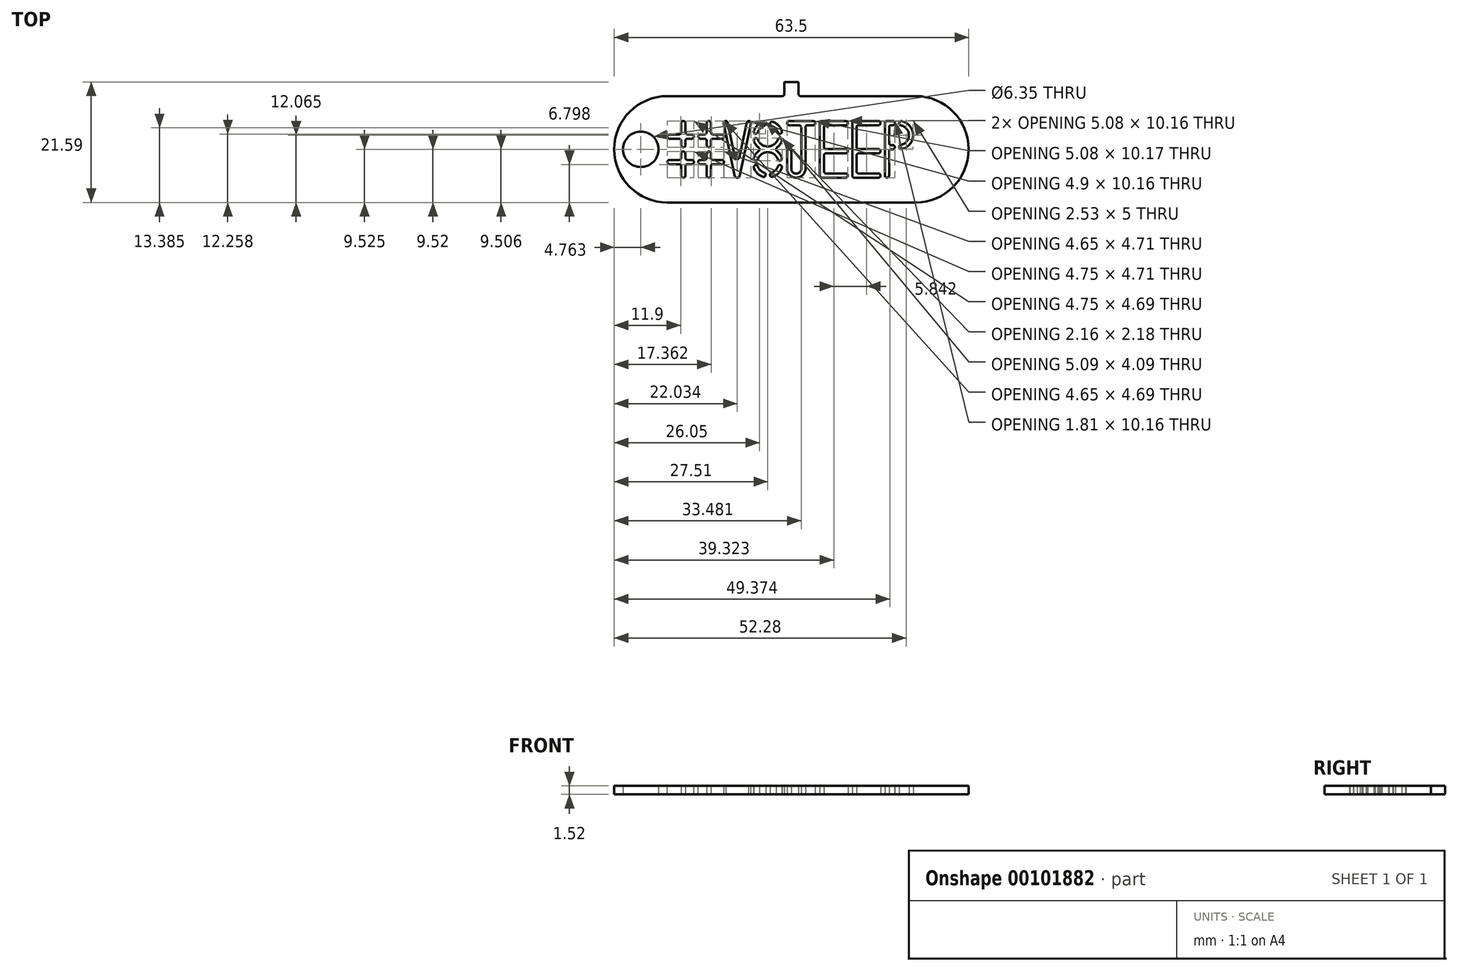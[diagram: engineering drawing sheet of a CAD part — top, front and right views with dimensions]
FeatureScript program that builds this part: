
annotation { "Feature Type Name" : "Feature", "Feature Type Description" : "" }
export const myFeature = defineFeature(function(context is Context, id is Id, definition is map)
    precondition{}
    {
        {
            var Q0;
            Q0=qCreatedBy(makeId("Top.planeOp"),FACE);
            var sketch = newSketch(context, id + "F0", { "sketchPlane" : qUnion([Q0])});
            skLineSegment(sketch, "E0.bottom", {"start": v(0, 0) * mm, "end": v(63.5, 0) * mm, "construction": true});
            skLineSegment(sketch, "E0.top", {"start": v(0, 19.05) * mm, "end": v(63.5, 19.05) * mm, "construction": true});
            skLineSegment(sketch, "E0.left", {"start": v(0, 0) * mm, "end": v(0, 19.05) * mm, "construction": true});
            skLineSegment(sketch, "E0.right", {"start": v(63.5, 0) * mm, "end": v(63.5, 19.05) * mm, "construction": true});
            skCircle(sketch, "E1", {"center": v(9.53, 9.53) * mm, "radius": 9.53 * mm, "construction": true});
            skCircle(sketch, "E2", {"center": v(53.97, 9.53) * mm, "radius": 9.53 * mm, "construction": true});
            skArc(sketch, "E3", {"start": v(9.52, 19.05) * mm, "mid": v(0, 9.53) * mm, "end": v(9.53, 0) * mm});
            skArc(sketch, "E4", {"start": v(53.97, 0) * mm, "mid": v(63.5, 9.53) * mm, "end": v(53.97, 19.05) * mm});
            skLineSegment(sketch, "E5", {"start": v(53.97, 0) * mm, "end": v(9.52, 0) * mm});
            skLineSegment(sketch, "E6.bottom", {"start": v(9.53, 12.2) * mm, "end": v(19.69, 12.2) * mm, "construction": true});
            skLineSegment(sketch, "E6.top", {"start": v(9.53, 11.44) * mm, "end": v(19.69, 11.44) * mm, "construction": true});
            skLineSegment(sketch, "E6.left", {"start": v(9.53, 12.2) * mm, "end": v(9.53, 11.44) * mm, "construction": true});
            skLineSegment(sketch, "E6.right", {"start": v(19.69, 12.2) * mm, "end": v(19.69, 11.44) * mm, "construction": true});
            skLineSegment(sketch, "E7.bottom", {"start": v(9.53, 7.63) * mm, "end": v(19.69, 7.63) * mm, "construction": true});
            skLineSegment(sketch, "E7.top", {"start": v(9.53, 6.86) * mm, "end": v(19.69, 6.86) * mm, "construction": true});
            skLineSegment(sketch, "E7.left", {"start": v(9.53, 7.63) * mm, "end": v(9.53, 6.86) * mm, "construction": true});
            skLineSegment(sketch, "E7.right", {"start": v(19.69, 7.63) * mm, "end": v(19.69, 6.86) * mm, "construction": true});
            skLineSegment(sketch, "E8.bottom", {"start": v(12, 14.6) * mm, "end": v(12.75, 14.6) * mm, "construction": true});
            skLineSegment(sketch, "E8.top", {"start": v(12, 4.44) * mm, "end": v(12.75, 4.44) * mm, "construction": true});
            skLineSegment(sketch, "E8.left", {"start": v(12, 14.6) * mm, "end": v(12, 4.44) * mm, "construction": true});
            skLineSegment(sketch, "E8.right", {"start": v(12.75, 14.6) * mm, "end": v(12.75, 4.44) * mm, "construction": true});
            skLineSegment(sketch, "E9.bottom", {"start": v(16.56, 14.6) * mm, "end": v(17.32, 14.6) * mm, "construction": true});
            skLineSegment(sketch, "E9.top", {"start": v(16.56, 4.44) * mm, "end": v(17.32, 4.44) * mm, "construction": true});
            skLineSegment(sketch, "E9.left", {"start": v(16.56, 14.6) * mm, "end": v(16.56, 4.44) * mm, "construction": true});
            skLineSegment(sketch, "E9.right", {"start": v(17.32, 14.6) * mm, "end": v(17.32, 4.44) * mm, "construction": true});
            skLineSegment(sketch, "E10", {"start": v(9.53, 14.6) * mm, "end": v(53.97, 14.6) * mm, "construction": true});
            skLineSegment(sketch, "E11", {"start": v(53.97, 9.53) * mm, "end": v(53.97, 14.6) * mm, "construction": true});
            skLineSegment(sketch, "E12", {"start": v(9.53, 14.6) * mm, "end": v(9.53, 9.53) * mm, "construction": true});
            skLineSegment(sketch, "E13", {"start": v(53.97, 9.53) * mm, "end": v(53.97, 4.45) * mm, "construction": true});
            skLineSegment(sketch, "E14", {"start": v(53.97, 4.45) * mm, "end": v(9.53, 4.45) * mm, "construction": true});
            skLineSegment(sketch, "E15", {"start": v(9.52, 9.53) * mm, "end": v(9.52, 4.45) * mm, "construction": true});
            skLineSegment(sketch, "E16", {"start": v(19.5, 14.6) * mm, "end": v(20.26, 14.6) * mm, "construction": true});
            skLineSegment(sketch, "E17", {"start": v(19.5, 14.6) * mm, "end": v(21.65, 4.44) * mm});
            skLineSegment(sketch, "E18", {"start": v(21.65, 4.45) * mm, "end": v(22.41, 4.45) * mm});
            skLineSegment(sketch, "E19", {"start": v(22.41, 4.44) * mm, "end": v(24.57, 14.6) * mm});
            skLineSegment(sketch, "E20", {"start": v(24.57, 14.6) * mm, "end": v(23.81, 14.6) * mm});
            skLineSegment(sketch, "E21", {"start": v(23.81, 14.6) * mm, "end": v(22.03, 6.32) * mm});
            skLineSegment(sketch, "E22", {"start": v(22.03, 6.32) * mm, "end": v(20.26, 14.6) * mm});
            skCircle(sketch, "E23", {"center": v(27.51, 11.94) * mm, "radius": 2.67 * mm, "construction": true});
            skCircle(sketch, "E24", {"center": v(27.51, 7.11) * mm, "radius": 2.67 * mm, "construction": true});
            skCircle(sketch, "E25", {"center": v(27.51, 11.94) * mm, "radius": 1.9 * mm, "construction": true});
            skCircle(sketch, "E26", {"center": v(27.51, 7.11) * mm, "radius": 1.9 * mm, "construction": true});
            skLineSegment(sketch, "E27", {"start": v(20.26, 14.6) * mm, "end": v(23.81, 14.6) * mm, "construction": true});
            skLineSegment(sketch, "E28", {"start": v(22.03, 14.6) * mm, "end": v(22.03, 4.45) * mm, "construction": true});
            skLineSegment(sketch, "E29", {"start": v(30.94, 14.6) * mm, "end": v(36.02, 14.6) * mm, "construction": true});
            skLineSegment(sketch, "E30", {"start": v(30.94, 14.6) * mm, "end": v(30.94, 4.44) * mm, "construction": true});
            skLineSegment(sketch, "E31", {"start": v(36.02, 14.6) * mm, "end": v(36.02, 4.44) * mm, "construction": true});
            skLineSegment(sketch, "E32", {"start": v(27.51, 14.6) * mm, "end": v(27.51, 4.44) * mm, "construction": true});
            skLineSegment(sketch, "E33", {"start": v(36.78, 14.6) * mm, "end": v(36.78, 4.44) * mm, "construction": true});
            skLineSegment(sketch, "E34", {"start": v(36.78, 4.45) * mm, "end": v(41.86, 4.45) * mm, "construction": true});
            skLineSegment(sketch, "E35", {"start": v(41.86, 4.44) * mm, "end": v(41.86, 14.6) * mm, "construction": true});
            skLineSegment(sketch, "E36", {"start": v(41.86, 14.6) * mm, "end": v(42.63, 14.6) * mm, "construction": true});
            skLineSegment(sketch, "E37", {"start": v(42.63, 14.6) * mm, "end": v(42.63, 4.44) * mm, "construction": true});
            skLineSegment(sketch, "E38", {"start": v(42.63, 4.45) * mm, "end": v(47.7, 4.45) * mm, "construction": true});
            skLineSegment(sketch, "E39", {"start": v(47.7, 4.44) * mm, "end": v(47.7, 14.6) * mm, "construction": true});
            skLineSegment(sketch, "E40", {"start": v(47.7, 14.6) * mm, "end": v(48.47, 14.6) * mm, "construction": true});
            skLineSegment(sketch, "E41", {"start": v(48.47, 14.6) * mm, "end": v(48.47, 4.44) * mm, "construction": true});
            skLineSegment(sketch, "E42", {"start": v(48.47, 4.45) * mm, "end": v(53.55, 4.45) * mm, "construction": true});
            skLineSegment(sketch, "E43", {"start": v(53.55, 4.44) * mm, "end": v(53.55, 14.6) * mm, "construction": true});
            skLineSegment(sketch, "E44", {"start": v(41.86, 13.84) * mm, "end": v(37.55, 13.84) * mm});
            skLineSegment(sketch, "E45", {"start": v(37.55, 13.84) * mm, "end": v(37.55, 9.56) * mm});
            skLineSegment(sketch, "E46", {"start": v(37.55, 9.56) * mm, "end": v(41.86, 9.56) * mm});
            skLineSegment(sketch, "E47", {"start": v(41.86, 9.56) * mm, "end": v(41.86, 8.8) * mm});
            skLineSegment(sketch, "E48", {"start": v(41.86, 8.8) * mm, "end": v(37.55, 8.8) * mm});
            skLineSegment(sketch, "E49", {"start": v(37.55, 8.8) * mm, "end": v(37.55, 5.2) * mm});
            skLineSegment(sketch, "E50", {"start": v(37.55, 5.2) * mm, "end": v(41.86, 5.2) * mm});
            skLineSegment(sketch, "E51", {"start": v(41.86, 5.2) * mm, "end": v(41.86, 4.45) * mm});
            skLineSegment(sketch, "E52", {"start": v(36.78, 4.44) * mm, "end": v(36.78, 14.6) * mm});
            skLineSegment(sketch, "E53", {"start": v(41.86, 14.6) * mm, "end": v(36.78, 14.6) * mm});
            skLineSegment(sketch, "E54", {"start": v(41.86, 14.6) * mm, "end": v(41.86, 13.84) * mm});
            skLineSegment(sketch, "E55", {"start": v(42.63, 14.6) * mm, "end": v(47.7, 14.6) * mm, "construction": true});
            skLineSegment(sketch, "E56", {"start": v(42.63, 14.6) * mm, "end": v(47.7, 14.6) * mm});
            skLineSegment(sketch, "E57", {"start": v(47.7, 13.84) * mm, "end": v(43.39, 13.84) * mm});
            skLineSegment(sketch, "E58", {"start": v(43.39, 13.84) * mm, "end": v(43.39, 9.56) * mm});
            skLineSegment(sketch, "E59", {"start": v(43.39, 9.56) * mm, "end": v(47.7, 9.56) * mm});
            skLineSegment(sketch, "E60", {"start": v(47.7, 9.56) * mm, "end": v(47.7, 8.8) * mm});
            skLineSegment(sketch, "E61", {"start": v(47.7, 8.8) * mm, "end": v(43.39, 8.8) * mm});
            skLineSegment(sketch, "E62", {"start": v(43.39, 8.8) * mm, "end": v(43.39, 5.2) * mm});
            skLineSegment(sketch, "E63", {"start": v(43.39, 5.2) * mm, "end": v(47.7, 5.2) * mm});
            skLineSegment(sketch, "E64", {"start": v(47.7, 5.2) * mm, "end": v(47.7, 4.45) * mm});
            skLineSegment(sketch, "E65", {"start": v(47.7, 4.45) * mm, "end": v(42.63, 4.44) * mm});
            skLineSegment(sketch, "E66", {"start": v(42.63, 4.44) * mm, "end": v(42.63, 14.6) * mm});
            skLineSegment(sketch, "E67", {"start": v(47.7, 13.84) * mm, "end": v(47.7, 14.6) * mm});
            skLineSegment(sketch, "E68", {"start": v(48.47, 4.44) * mm, "end": v(48.47, 14.6) * mm});
            skLineSegment(sketch, "E69", {"start": v(48.47, 14.6) * mm, "end": v(53.55, 14.6) * mm, "construction": true});
            skLineSegment(sketch, "E70", {"start": v(48.47, 4.45) * mm, "end": v(49.23, 4.45) * mm});
            skLineSegment(sketch, "E71", {"start": v(49.23, 4.44) * mm, "end": v(49.23, 9.52) * mm});
            skLineSegment(sketch, "E72", {"start": v(51, 14.6) * mm, "end": v(51, 9.52) * mm, "construction": true});
            skLineSegment(sketch, "E73", {"start": v(51, 9.52) * mm, "end": v(49.23, 9.52) * mm, "construction": true});
            skArc(sketch, "E74", {"start": v(51, 9.52) * mm, "mid": v(53.55, 12.06) * mm, "end": v(51, 14.6) * mm});
            skLineSegment(sketch, "E75", {"start": v(49.23, 13.84) * mm, "end": v(49.23, 10.29) * mm});
            skLineSegment(sketch, "E76", {"start": v(51, 10.29) * mm, "end": v(51, 13.84) * mm, "construction": true});
            skArc(sketch, "E77", {"start": v(51, 10.29) * mm, "mid": v(52.79, 12.06) * mm, "end": v(51, 13.84) * mm});
            skLineSegment(sketch, "E78", {"start": v(30.94, 9.52) * mm, "end": v(31.7, 9.52) * mm});
            skLineSegment(sketch, "E79", {"start": v(31.7, 9.52) * mm, "end": v(31.7, 5.83) * mm});
            skLineSegment(sketch, "E80", {"start": v(30.94, 5.83) * mm, "end": v(36.02, 5.83) * mm, "construction": true});
            skLineSegment(sketch, "E81", {"start": v(33.48, 5.83) * mm, "end": v(33.48, 13.84) * mm});
            skLineSegment(sketch, "E82", {"start": v(34.24, 5.83) * mm, "end": v(34.24, 13.84) * mm});
            skArc(sketch, "E83", {"start": v(30.94, 5.83) * mm, "mid": v(32.6, 4.43) * mm, "end": v(34.24, 5.83) * mm});
            skArc(sketch, "E84", {"start": v(31.7, 5.83) * mm, "mid": v(32.6, 5.17) * mm, "end": v(33.48, 5.83) * mm});
            skLineSegment(sketch, "E85", {"start": v(30.94, 14.6) * mm, "end": v(36.02, 14.6) * mm});
            skLineSegment(sketch, "E86", {"start": v(30.94, 13.84) * mm, "end": v(36.02, 13.84) * mm, "construction": true});
            skLineSegment(sketch, "E87", {"start": v(30.94, 9.52) * mm, "end": v(30.94, 5.83) * mm});
            skLineSegment(sketch, "E88", {"start": v(34.24, 13.84) * mm, "end": v(36.02, 13.84) * mm});
            skLineSegment(sketch, "E89", {"start": v(36.02, 14.6) * mm, "end": v(36.02, 13.84) * mm});
            skLineSegment(sketch, "E90", {"start": v(30.94, 14.6) * mm, "end": v(30.94, 13.84) * mm});
            skLineSegment(sketch, "E91", {"start": v(33.48, 13.84) * mm, "end": v(30.94, 13.84) * mm});
            skLineSegment(sketch, "E92", {"start": v(12, 14.6) * mm, "end": v(12, 12.2) * mm});
            skLineSegment(sketch, "E93", {"start": v(12, 12.2) * mm, "end": v(9.53, 12.2) * mm});
            skLineSegment(sketch, "E94", {"start": v(9.53, 11.44) * mm, "end": v(12, 11.44) * mm});
            skLineSegment(sketch, "E95", {"start": v(12, 11.44) * mm, "end": v(12, 9.91) * mm});
            skLineSegment(sketch, "E96", {"start": v(12, 14.6) * mm, "end": v(12.75, 14.6) * mm});
            skLineSegment(sketch, "E97", {"start": v(12.75, 12.2) * mm, "end": v(14.28, 12.2) * mm});
            skLineSegment(sketch, "E98", {"start": v(12, 7.63) * mm, "end": v(9.53, 7.63) * mm});
            skLineSegment(sketch, "E99", {"start": v(9.53, 7.63) * mm, "end": v(9.53, 6.86) * mm});
            skLineSegment(sketch, "E100", {"start": v(9.53, 6.86) * mm, "end": v(12, 6.86) * mm});
            skLineSegment(sketch, "E101", {"start": v(12, 6.86) * mm, "end": v(12, 4.44) * mm});
            skLineSegment(sketch, "E102", {"start": v(12.75, 4.44) * mm, "end": v(12.75, 6.86) * mm});
            skLineSegment(sketch, "E103", {"start": v(12.75, 6.86) * mm, "end": v(14.28, 6.86) * mm});
            skLineSegment(sketch, "E104", {"start": v(15.04, 6.86) * mm, "end": v(16.56, 6.86) * mm});
            skLineSegment(sketch, "E105", {"start": v(16.56, 6.86) * mm, "end": v(16.56, 4.44) * mm});
            skLineSegment(sketch, "E106", {"start": v(17.32, 4.44) * mm, "end": v(17.32, 6.86) * mm});
            skLineSegment(sketch, "E107", {"start": v(17.32, 6.86) * mm, "end": v(19.69, 6.86) * mm});
            skLineSegment(sketch, "E108", {"start": v(19.69, 7.63) * mm, "end": v(19.69, 6.86) * mm});
            skLineSegment(sketch, "E109", {"start": v(19.69, 7.63) * mm, "end": v(17.32, 7.63) * mm});
            skLineSegment(sketch, "E110", {"start": v(17.32, 7.63) * mm, "end": v(17.32, 9.15) * mm});
            skLineSegment(sketch, "E111", {"start": v(12, 7.63) * mm, "end": v(12, 9.15) * mm});
            skLineSegment(sketch, "E112", {"start": v(12.75, 14.6) * mm, "end": v(12.75, 12.2) * mm});
            skLineSegment(sketch, "E113", {"start": v(16.56, 14.6) * mm, "end": v(16.56, 12.2) * mm});
            skLineSegment(sketch, "E114", {"start": v(16.56, 12.2) * mm, "end": v(15.04, 12.2) * mm});
            skLineSegment(sketch, "E115", {"start": v(17.32, 14.6) * mm, "end": v(17.32, 12.2) * mm});
            skLineSegment(sketch, "E116", {"start": v(17.32, 12.2) * mm, "end": v(19.69, 12.2) * mm});
            skLineSegment(sketch, "E117", {"start": v(19.69, 11.44) * mm, "end": v(17.32, 11.44) * mm});
            skLineSegment(sketch, "E118", {"start": v(17.32, 11.44) * mm, "end": v(17.32, 9.91) * mm});
            skLineSegment(sketch, "E119", {"start": v(12.75, 11.44) * mm, "end": v(14.28, 11.44) * mm});
            skLineSegment(sketch, "E120", {"start": v(12.75, 9.91) * mm, "end": v(12.75, 11.44) * mm});
            skLineSegment(sketch, "E121", {"start": v(12.75, 7.63) * mm, "end": v(12.75, 9.15) * mm});
            skLineSegment(sketch, "E122", {"start": v(12.75, 7.63) * mm, "end": v(14.28, 7.63) * mm});
            skLineSegment(sketch, "E123", {"start": v(16.56, 11.44) * mm, "end": v(15.04, 11.44) * mm});
            skLineSegment(sketch, "E124", {"start": v(16.56, 11.44) * mm, "end": v(16.56, 9.91) * mm});
            skLineSegment(sketch, "E125", {"start": v(16.56, 7.63) * mm, "end": v(16.56, 9.15) * mm});
            skLineSegment(sketch, "E126", {"start": v(16.56, 7.63) * mm, "end": v(15.04, 7.63) * mm});
            skLineSegment(sketch, "E127", {"start": v(27.13, 14.58) * mm, "end": v(27.13, 13.8) * mm});
            skLineSegment(sketch, "E128", {"start": v(19.5, 14.6) * mm, "end": v(20.26, 14.6) * mm});
            skLineSegment(sketch, "E129", {"start": v(36.78, 4.44) * mm, "end": v(41.86, 4.44) * mm});
            skLineSegment(sketch, "E130", {"start": v(48.47, 14.6) * mm, "end": v(50.28, 14.6) * mm});
            skLineSegment(sketch, "E131", {"start": v(51, 14.6) * mm, "end": v(51, 13.84) * mm});
            skLineSegment(sketch, "E132", {"start": v(50.28, 14.6) * mm, "end": v(50.28, 13.84) * mm});
            skLineSegment(sketch, "E133", {"start": v(50.28, 13.84) * mm, "end": v(49.23, 13.84) * mm});
            skLineSegment(sketch, "E134", {"start": v(49.23, 10.29) * mm, "end": v(50.26, 10.29) * mm});
            skLineSegment(sketch, "E135", {"start": v(50.26, 10.29) * mm, "end": v(50.26, 9.52) * mm});
            skLineSegment(sketch, "E136", {"start": v(50.26, 9.52) * mm, "end": v(49.23, 9.52) * mm});
            skLineSegment(sketch, "E137", {"start": v(51, 10.29) * mm, "end": v(51, 9.52) * mm});
            skLineSegment(sketch, "E138", {"start": v(27.9, 13.8) * mm, "end": v(27.9, 14.58) * mm});
            skLineSegment(sketch, "E139", {"start": v(27.13, 5.25) * mm, "end": v(27.13, 4.47) * mm});
            skLineSegment(sketch, "E140", {"start": v(27.9, 5.25) * mm, "end": v(27.9, 4.47) * mm});
            skLineSegment(sketch, "E141", {"start": v(19.69, 12.2) * mm, "end": v(19.69, 11.44) * mm});
            skLineSegment(sketch, "E142", {"start": v(16.56, 14.6) * mm, "end": v(17.32, 14.6) * mm});
            skLineSegment(sketch, "E143", {"start": v(9.53, 12.2) * mm, "end": v(9.53, 11.44) * mm});
            skLineSegment(sketch, "E144", {"start": v(16.56, 4.44) * mm, "end": v(17.32, 4.44) * mm});
            skLineSegment(sketch, "E145", {"start": v(12, 4.44) * mm, "end": v(12.75, 4.44) * mm});
            skLineSegment(sketch, "E146", {"start": v(14.28, 7.63) * mm, "end": v(14.28, 6.86) * mm});
            skLineSegment(sketch, "E147", {"start": v(15.04, 7.63) * mm, "end": v(15.04, 6.86) * mm});
            skLineSegment(sketch, "E148", {"start": v(16.56, 9.15) * mm, "end": v(17.32, 9.15) * mm});
            skLineSegment(sketch, "E149", {"start": v(16.56, 9.91) * mm, "end": v(17.32, 9.91) * mm});
            skLineSegment(sketch, "E150", {"start": v(12, 9.91) * mm, "end": v(12.75, 9.91) * mm});
            skLineSegment(sketch, "E151", {"start": v(12.75, 9.15) * mm, "end": v(12, 9.15) * mm});
            skLineSegment(sketch, "E152", {"start": v(14.28, 11.44) * mm, "end": v(14.28, 12.2) * mm});
            skLineSegment(sketch, "E153", {"start": v(15.04, 12.2) * mm, "end": v(15.04, 11.44) * mm});
            skLineSegment(sketch, "E154", {"start": v(24.87, 12.3) * mm, "end": v(25.64, 12.3) * mm});
            skLineSegment(sketch, "E155", {"start": v(24.88, 11.53) * mm, "end": v(25.65, 11.53) * mm});
            skLineSegment(sketch, "E156", {"start": v(27.51, 11.94) * mm, "end": v(24.85, 11.94) * mm, "construction": true});
            skLineSegment(sketch, "E157", {"start": v(27.51, 11.94) * mm, "end": v(30.18, 11.94) * mm, "construction": true});
            skLineSegment(sketch, "E158", {"start": v(27.51, 7.11) * mm, "end": v(24.85, 7.11) * mm, "construction": true});
            skLineSegment(sketch, "E159", {"start": v(27.51, 7.11) * mm, "end": v(30.18, 7.11) * mm, "construction": true});
            skLineSegment(sketch, "E160", {"start": v(29.38, 12.31) * mm, "end": v(30.15, 12.31) * mm});
            skLineSegment(sketch, "E161", {"start": v(29.38, 11.55) * mm, "end": v(30.15, 11.55) * mm});
            skArc(sketch, "E162", {"start": v(27.13, 14.58) * mm, "mid": v(25.62, 13.82) * mm, "end": v(24.87, 12.3) * mm});
            skArc(sketch, "E163", {"start": v(30.15, 12.31) * mm, "mid": v(29.4, 13.82) * mm, "end": v(27.9, 14.58) * mm});
            skArc(sketch, "E164", {"start": v(28.65, 9.53) * mm, "mid": v(29.65, 10.35) * mm, "end": v(30.15, 11.55) * mm});
            skArc(sketch, "E165", {"start": v(24.88, 11.53) * mm, "mid": v(25.38, 10.34) * mm, "end": v(26.38, 9.53) * mm});
            skArc(sketch, "E166", {"start": v(25.65, 11.53) * mm, "mid": v(27.52, 10.03) * mm, "end": v(29.38, 11.55) * mm});
            skArc(sketch, "E167", {"start": v(27.13, 13.8) * mm, "mid": v(26.16, 13.28) * mm, "end": v(25.64, 12.3) * mm});
            skArc(sketch, "E168", {"start": v(29.38, 12.31) * mm, "mid": v(28.86, 13.28) * mm, "end": v(27.9, 13.8) * mm});
            skLineSegment(sketch, "E169", {"start": v(24.87, 7.46) * mm, "end": v(25.64, 7.46) * mm});
            skLineSegment(sketch, "E170", {"start": v(25.65, 6.7) * mm, "end": v(24.88, 6.7) * mm});
            skLineSegment(sketch, "E171", {"start": v(29.38, 7.47) * mm, "end": v(30.15, 7.47) * mm});
            skLineSegment(sketch, "E172", {"start": v(30.15, 6.71) * mm, "end": v(29.38, 6.71) * mm});
            skArc(sketch, "E173", {"start": v(29.38, 7.47) * mm, "mid": v(27.5, 9.02) * mm, "end": v(25.64, 7.46) * mm});
            skArc(sketch, "E174", {"start": v(26.38, 9.52) * mm, "mid": v(25.36, 8.69) * mm, "end": v(24.87, 7.46) * mm});
            skArc(sketch, "E175", {"start": v(27.9, 4.47) * mm, "mid": v(29.4, 5.22) * mm, "end": v(30.15, 6.71) * mm});
            skArc(sketch, "E176", {"start": v(27.9, 5.25) * mm, "mid": v(28.85, 5.76) * mm, "end": v(29.38, 6.71) * mm});
            skArc(sketch, "E177", {"start": v(25.65, 6.7) * mm, "mid": v(26.18, 5.75) * mm, "end": v(27.13, 5.25) * mm});
            skArc(sketch, "E178", {"start": v(24.88, 6.7) * mm, "mid": v(25.64, 5.21) * mm, "end": v(27.13, 4.47) * mm});
            skArc(sketch, "E179", {"start": v(30.15, 7.47) * mm, "mid": v(29.66, 8.7) * mm, "end": v(28.65, 9.52) * mm});
            skCircle(sketch, "E180", {"center": v(4.76, 9.52) * mm, "radius": 3.18 * mm});
            skLineSegment(sketch, "E181", {"start": v(9.52, 9.52) * mm, "end": v(0, 9.52) * mm, "construction": true});
            skLineSegment(sketch, "E182", {"start": v(31.75, 19.05) * mm, "end": v(31.75, 21.6) * mm, "construction": true});
            skLineSegment(sketch, "E183", {"start": v(30.48, 21.59) * mm, "end": v(33.02, 21.59) * mm});
            skLineSegment(sketch, "E184", {"start": v(30.48, 21.59) * mm, "end": v(30.48, 19.05) * mm});
            skLineSegment(sketch, "E185", {"start": v(33.02, 21.59) * mm, "end": v(33.02, 19.05) * mm});
            skLineSegment(sketch, "E186", {"start": v(9.52, 19.05) * mm, "end": v(30.48, 19.05) * mm});
            skLineSegment(sketch, "E187", {"start": v(53.97, 19.05) * mm, "end": v(33.02, 19.05) * mm});
            skSolve(sketch);
        }
        {
            var Q0;
            Q0 = qSketchRegion(id + "F0", true);
            var Q1;
            Q1=makeQuery(id+"F0.imprint","IMPRINT",FACE,{"disambiguationData":[TD([[makeQuery(id+"F0.imprint","IMPRINT",EDGE,{"derivedFrom":sQuery(id+"F0.wireOp",EDGE,"E3")}),1.0]])]});
            extrude(context, id + "F1", {"entities" : qUnion([Q0, Q1]), "depth" : 1.52 * mm});
        }
        {
            var Q0;
            Q0=makeQuery(id+"F1.opExtrude","SWEPT_EDGE",EDGE,{"disambiguationData":[OSD([sQuery(id+"F0.wireOp",EDGE,"E19"),sQuery(id+"F0.wireOp",EDGE,"E20")])]});
            var Q1;
            Q1=makeQuery(id+"F1.opExtrude","SWEPT_EDGE",EDGE,{"disambiguationData":[OSD([sQuery(id+"F0.wireOp",EDGE,"E22"),sQuery(id+"F0.wireOp",EDGE,"E128")])]});
            var Q2;
            Q2=makeQuery(id+"F1.opExtrude","SWEPT_EDGE",EDGE,{"disambiguationData":[OSD([sQuery(id+"F0.wireOp",EDGE,"E20"),sQuery(id+"F0.wireOp",EDGE,"E21")])]});
            var Q3;
            Q3=makeQuery(id+"F1.opExtrude","SWEPT_EDGE",EDGE,{"disambiguationData":[OSD([sQuery(id+"F0.wireOp",EDGE,"E17"),sQuery(id+"F0.wireOp",EDGE,"E128")])]});
            var Q4;
            Q4=makeQuery(id+"F1.opExtrude","SWEPT_EDGE",EDGE,{"disambiguationData":[OSD([sQuery(id+"F0.wireOp",EDGE,"E21"),sQuery(id+"F0.wireOp",EDGE,"E22")])]});
            var Q5;
            Q5=makeQuery(id+"F1.opExtrude","SWEPT_EDGE",EDGE,{"disambiguationData":[OSD([sQuery(id+"F0.wireOp",EDGE,"E17"),sQuery(id+"F0.wireOp",EDGE,"E18")])]});
            var Q6;
            Q6=makeQuery(id+"F1.opExtrude","SWEPT_EDGE",EDGE,{"disambiguationData":[OSD([sQuery(id+"F0.wireOp",EDGE,"E18"),sQuery(id+"F0.wireOp",EDGE,"E19")])]});
            var Q7;
            Q7=makeQuery(id+"F1.opExtrude","SWEPT_EDGE",EDGE,{"disambiguationData":[OSD([sQuery(id+"F0.wireOp",EDGE,"E85"),sQuery(id+"F0.wireOp",EDGE,"E89")])]});
            var Q8;
            Q8=makeQuery(id+"F1.opExtrude","SWEPT_EDGE",EDGE,{"disambiguationData":[OSD([sQuery(id+"F0.wireOp",EDGE,"E88"),sQuery(id+"F0.wireOp",EDGE,"E89")])]});
            var Q9;
            Q9=makeQuery(id+"F1.opExtrude","SWEPT_EDGE",EDGE,{"disambiguationData":[OSD([sQuery(id+"F0.wireOp",EDGE,"E90"),sQuery(id+"F0.wireOp",EDGE,"E91")])]});
            var Q10;
            Q10=makeQuery(id+"F1.opExtrude","SWEPT_EDGE",EDGE,{"disambiguationData":[OSD([sQuery(id+"F0.wireOp",EDGE,"E81"),sQuery(id+"F0.wireOp",EDGE,"E91")])]});
            var Q11;
            Q11=makeQuery(id+"F1.opExtrude","SWEPT_EDGE",EDGE,{"disambiguationData":[OSD([sQuery(id+"F0.wireOp",EDGE,"E82"),sQuery(id+"F0.wireOp",EDGE,"E88")])]});
            var Q12;
            Q12=makeQuery(id+"F1.opExtrude","SWEPT_EDGE",EDGE,{"disambiguationData":[OSD([sQuery(id+"F0.wireOp",EDGE,"E85"),sQuery(id+"F0.wireOp",EDGE,"E90")])]});
            var Q13;
            Q13=makeQuery(id+"F1.opExtrude","SWEPT_EDGE",EDGE,{"disambiguationData":[OSD([sQuery(id+"F0.wireOp",EDGE,"E78"),sQuery(id+"F0.wireOp",EDGE,"E87")])]});
            var Q14;
            Q14=makeQuery(id+"F1.opExtrude","SWEPT_EDGE",EDGE,{"disambiguationData":[OSD([sQuery(id+"F0.wireOp",EDGE,"E78"),sQuery(id+"F0.wireOp",EDGE,"E79")])]});
            var Q15;
            Q15=makeQuery(id+"F1.opExtrude","SWEPT_EDGE",EDGE,{"disambiguationData":[OSD([sQuery(id+"F0.wireOp",EDGE,"E53"),sQuery(id+"F0.wireOp",EDGE,"E54")])]});
            var Q16;
            Q16=makeQuery(id+"F1.opExtrude","SWEPT_EDGE",EDGE,{"disambiguationData":[OSD([sQuery(id+"F0.wireOp",EDGE,"E46"),sQuery(id+"F0.wireOp",EDGE,"E47")])]});
            var Q17;
            Q17=makeQuery(id+"F1.opExtrude","SWEPT_EDGE",EDGE,{"disambiguationData":[OSD([sQuery(id+"F0.wireOp",EDGE,"E50"),sQuery(id+"F0.wireOp",EDGE,"E51")])]});
            var Q18;
            Q18=makeQuery(id+"F1.opExtrude","SWEPT_EDGE",EDGE,{"disambiguationData":[OSD([sQuery(id+"F0.wireOp",EDGE,"E49"),sQuery(id+"F0.wireOp",EDGE,"E50")])]});
            var Q19;
            Q19=makeQuery(id+"F1.opExtrude","SWEPT_EDGE",EDGE,{"disambiguationData":[OSD([sQuery(id+"F0.wireOp",EDGE,"E45"),sQuery(id+"F0.wireOp",EDGE,"E46")])]});
            var Q20;
            Q20=makeQuery(id+"F1.opExtrude","SWEPT_EDGE",EDGE,{"disambiguationData":[OSD([sQuery(id+"F0.wireOp",EDGE,"E48"),sQuery(id+"F0.wireOp",EDGE,"E49")])]});
            var Q21;
            Q21=makeQuery(id+"F1.opExtrude","SWEPT_EDGE",EDGE,{"disambiguationData":[OSD([sQuery(id+"F0.wireOp",EDGE,"E44"),sQuery(id+"F0.wireOp",EDGE,"E45")])]});
            var Q22;
            Q22=makeQuery(id+"F1.opExtrude","SWEPT_EDGE",EDGE,{"disambiguationData":[OSD([sQuery(id+"F0.wireOp",EDGE,"E52"),sQuery(id+"F0.wireOp",EDGE,"E53")])]});
            var Q23;
            Q23=makeQuery(id+"F1.opExtrude","SWEPT_EDGE",EDGE,{"disambiguationData":[OSD([sQuery(id+"F0.wireOp",EDGE,"E52"),sQuery(id+"F0.wireOp",EDGE,"E129")])]});
            var Q24;
            Q24=makeQuery(id+"F1.opExtrude","SWEPT_EDGE",EDGE,{"disambiguationData":[OSD([sQuery(id+"F0.wireOp",EDGE,"E65"),sQuery(id+"F0.wireOp",EDGE,"E66")])]});
            var Q25;
            Q25=makeQuery(id+"F1.opExtrude","SWEPT_EDGE",EDGE,{"disambiguationData":[OSD([sQuery(id+"F0.wireOp",EDGE,"E51"),sQuery(id+"F0.wireOp",EDGE,"E129")])]});
            var Q26;
            Q26=makeQuery(id+"F1.opExtrude","SWEPT_EDGE",EDGE,{"disambiguationData":[OSD([sQuery(id+"F0.wireOp",EDGE,"E47"),sQuery(id+"F0.wireOp",EDGE,"E48")])]});
            var Q27;
            Q27=makeQuery(id+"F1.opExtrude","SWEPT_EDGE",EDGE,{"disambiguationData":[OSD([sQuery(id+"F0.wireOp",EDGE,"E44"),sQuery(id+"F0.wireOp",EDGE,"E54")])]});
            var Q28;
            Q28=makeQuery(id+"F1.opExtrude","SWEPT_EDGE",EDGE,{"disambiguationData":[OSD([sQuery(id+"F0.wireOp",EDGE,"E57"),sQuery(id+"F0.wireOp",EDGE,"E58")])]});
            var Q29;
            Q29=makeQuery(id+"F1.opExtrude","SWEPT_EDGE",EDGE,{"disambiguationData":[OSD([sQuery(id+"F0.wireOp",EDGE,"E58"),sQuery(id+"F0.wireOp",EDGE,"E59")])]});
            var Q30;
            Q30=makeQuery(id+"F1.opExtrude","SWEPT_EDGE",EDGE,{"disambiguationData":[OSD([sQuery(id+"F0.wireOp",EDGE,"E61"),sQuery(id+"F0.wireOp",EDGE,"E62")])]});
            var Q31;
            Q31=makeQuery(id+"F1.opExtrude","SWEPT_EDGE",EDGE,{"disambiguationData":[OSD([sQuery(id+"F0.wireOp",EDGE,"E62"),sQuery(id+"F0.wireOp",EDGE,"E63")])]});
            var Q32;
            Q32=makeQuery(id+"F1.opExtrude","SWEPT_EDGE",EDGE,{"disambiguationData":[OSD([sQuery(id+"F0.wireOp",EDGE,"E64"),sQuery(id+"F0.wireOp",EDGE,"E65")])]});
            var Q33;
            Q33=makeQuery(id+"F1.opExtrude","SWEPT_EDGE",EDGE,{"disambiguationData":[OSD([sQuery(id+"F0.wireOp",EDGE,"E60"),sQuery(id+"F0.wireOp",EDGE,"E61")])]});
            var Q34;
            Q34=makeQuery(id+"F1.opExtrude","SWEPT_EDGE",EDGE,{"disambiguationData":[OSD([sQuery(id+"F0.wireOp",EDGE,"E57"),sQuery(id+"F0.wireOp",EDGE,"E67")])]});
            var Q35;
            Q35=makeQuery(id+"F1.opExtrude","SWEPT_EDGE",EDGE,{"disambiguationData":[OSD([sQuery(id+"F0.wireOp",EDGE,"E56"),sQuery(id+"F0.wireOp",EDGE,"E66")])]});
            var Q36;
            Q36=makeQuery(id+"F1.opExtrude","SWEPT_EDGE",EDGE,{"disambiguationData":[OSD([sQuery(id+"F0.wireOp",EDGE,"E63"),sQuery(id+"F0.wireOp",EDGE,"E64")])]});
            var Q37;
            Q37=makeQuery(id+"F1.opExtrude","SWEPT_EDGE",EDGE,{"disambiguationData":[OSD([sQuery(id+"F0.wireOp",EDGE,"E59"),sQuery(id+"F0.wireOp",EDGE,"E60")])]});
            var Q38;
            Q38=makeQuery(id+"F1.opExtrude","SWEPT_EDGE",EDGE,{"disambiguationData":[OSD([sQuery(id+"F0.wireOp",EDGE,"E56"),sQuery(id+"F0.wireOp",EDGE,"E67")])]});
            var Q39;
            Q39=makeQuery(id+"F1.opExtrude","SWEPT_EDGE",EDGE,{"disambiguationData":[OSD([sQuery(id+"F0.wireOp",EDGE,"E130"),sQuery(id+"F0.wireOp",EDGE,"E132")])]});
            var Q40;
            Q40=makeQuery(id+"F1.opExtrude","SWEPT_EDGE",EDGE,{"disambiguationData":[OSD([sQuery(id+"F0.wireOp",EDGE,"E134"),sQuery(id+"F0.wireOp",EDGE,"E135")])]});
            var Q41;
            Q41=makeQuery(id+"F1.opExtrude","SWEPT_EDGE",EDGE,{"disambiguationData":[OSD([sQuery(id+"F0.wireOp",EDGE,"E135"),sQuery(id+"F0.wireOp",EDGE,"E136")])]});
            var Q42;
            Q42=makeQuery(id+"F1.opExtrude","SWEPT_EDGE",EDGE,{"disambiguationData":[OSD([sQuery(id+"F0.wireOp",EDGE,"E70"),sQuery(id+"F0.wireOp",EDGE,"E71")])]});
            var Q43;
            Q43=makeQuery(id+"F1.opExtrude","SWEPT_EDGE",EDGE,{"disambiguationData":[OSD([sQuery(id+"F0.wireOp",EDGE,"E74"),sQuery(id+"F0.wireOp",EDGE,"E137")])]});
            var Q44;
            Q44=makeQuery(id+"F1.opExtrude","SWEPT_EDGE",EDGE,{"disambiguationData":[OSD([sQuery(id+"F0.wireOp",EDGE,"E77"),sQuery(id+"F0.wireOp",EDGE,"E131")])]});
            var Q45;
            Q45=makeQuery(id+"F1.opExtrude","SWEPT_EDGE",EDGE,{"disambiguationData":[OSD([sQuery(id+"F0.wireOp",EDGE,"E77"),sQuery(id+"F0.wireOp",EDGE,"E137")])]});
            var Q46;
            Q46=makeQuery(id+"F1.opExtrude","SWEPT_EDGE",EDGE,{"disambiguationData":[OSD([sQuery(id+"F0.wireOp",EDGE,"E74"),sQuery(id+"F0.wireOp",EDGE,"E131")])]});
            var Q47;
            Q47=makeQuery(id+"F1.opExtrude","SWEPT_EDGE",EDGE,{"disambiguationData":[OSD([sQuery(id+"F0.wireOp",EDGE,"E68"),sQuery(id+"F0.wireOp",EDGE,"E130")])]});
            var Q48;
            Q48=makeQuery(id+"F1.opExtrude","SWEPT_EDGE",EDGE,{"disambiguationData":[OSD([sQuery(id+"F0.wireOp",EDGE,"E68"),sQuery(id+"F0.wireOp",EDGE,"E70")])]});
            var Q49;
            Q49=makeQuery(id+"F1.opExtrude","SWEPT_EDGE",EDGE,{"disambiguationData":[OSD([sQuery(id+"F0.wireOp",EDGE,"E171"),sQuery(id+"F0.wireOp",EDGE,"E173")])]});
            var Q50;
            Q50=makeQuery(id+"F1.opExtrude","SWEPT_EDGE",EDGE,{"disambiguationData":[OSD([sQuery(id+"F0.wireOp",EDGE,"E171"),sQuery(id+"F0.wireOp",EDGE,"E179")])]});
            var Q51;
            Q51=makeQuery(id+"F1.opExtrude","SWEPT_EDGE",EDGE,{"disambiguationData":[OSD([sQuery(id+"F0.wireOp",EDGE,"E172"),sQuery(id+"F0.wireOp",EDGE,"E175")])]});
            var Q52;
            Q52=makeQuery(id+"F1.opExtrude","SWEPT_EDGE",EDGE,{"disambiguationData":[OSD([sQuery(id+"F0.wireOp",EDGE,"E140"),sQuery(id+"F0.wireOp",EDGE,"E175")])]});
            var Q53;
            Q53=makeQuery(id+"F1.opExtrude","SWEPT_EDGE",EDGE,{"disambiguationData":[OSD([sQuery(id+"F0.wireOp",EDGE,"E140"),sQuery(id+"F0.wireOp",EDGE,"E176")])]});
            var Q54;
            Q54=makeQuery(id+"F1.opExtrude","SWEPT_EDGE",EDGE,{"disambiguationData":[OSD([sQuery(id+"F0.wireOp",EDGE,"E172"),sQuery(id+"F0.wireOp",EDGE,"E176")])]});
            var Q55;
            Q55=makeQuery(id+"F1.opExtrude","SWEPT_EDGE",EDGE,{"disambiguationData":[OSD([sQuery(id+"F0.wireOp",EDGE,"E170"),sQuery(id+"F0.wireOp",EDGE,"E177")])]});
            var Q56;
            Q56=makeQuery(id+"F1.opExtrude","SWEPT_EDGE",EDGE,{"disambiguationData":[OSD([sQuery(id+"F0.wireOp",EDGE,"E139"),sQuery(id+"F0.wireOp",EDGE,"E177")])]});
            var Q57;
            Q57=makeQuery(id+"F1.opExtrude","SWEPT_EDGE",EDGE,{"disambiguationData":[OSD([sQuery(id+"F0.wireOp",EDGE,"E139"),sQuery(id+"F0.wireOp",EDGE,"E178")])]});
            var Q58;
            Q58=makeQuery(id+"F1.opExtrude","SWEPT_EDGE",EDGE,{"disambiguationData":[OSD([sQuery(id+"F0.wireOp",EDGE,"E170"),sQuery(id+"F0.wireOp",EDGE,"E178")])]});
            var Q59;
            Q59=makeQuery(id+"F1.opExtrude","SWEPT_EDGE",EDGE,{"disambiguationData":[OSD([sQuery(id+"F0.wireOp",EDGE,"E169"),sQuery(id+"F0.wireOp",EDGE,"E173")])]});
            var Q60;
            Q60=makeQuery(id+"F1.opExtrude","SWEPT_EDGE",EDGE,{"disambiguationData":[OSD([sQuery(id+"F0.wireOp",EDGE,"E169"),sQuery(id+"F0.wireOp",EDGE,"E174")])]});
            var Q61;
            Q61=makeQuery(id+"F1.opExtrude","SWEPT_EDGE",EDGE,{"disambiguationData":[OSD([sQuery(id+"F0.wireOp",EDGE,"E165"),sQuery(id+"F0.wireOp",EDGE,"E174")])]});
            var Q62;
            Q62=makeQuery(id+"F1.opExtrude","SWEPT_EDGE",EDGE,{"disambiguationData":[OSD([sQuery(id+"F0.wireOp",EDGE,"E164"),sQuery(id+"F0.wireOp",EDGE,"E179")])]});
            var Q63;
            Q63=makeQuery(id+"F1.opExtrude","SWEPT_EDGE",EDGE,{"disambiguationData":[OSD([sQuery(id+"F0.wireOp",EDGE,"E155"),sQuery(id+"F0.wireOp",EDGE,"E165")])]});
            var Q64;
            Q64=makeQuery(id+"F1.opExtrude","SWEPT_EDGE",EDGE,{"disambiguationData":[OSD([sQuery(id+"F0.wireOp",EDGE,"E155"),sQuery(id+"F0.wireOp",EDGE,"E166")])]});
            var Q65;
            Q65=makeQuery(id+"F1.opExtrude","SWEPT_EDGE",EDGE,{"disambiguationData":[OSD([sQuery(id+"F0.wireOp",EDGE,"E161"),sQuery(id+"F0.wireOp",EDGE,"E166")])]});
            var Q66;
            Q66=makeQuery(id+"F1.opExtrude","SWEPT_EDGE",EDGE,{"disambiguationData":[OSD([sQuery(id+"F0.wireOp",EDGE,"E161"),sQuery(id+"F0.wireOp",EDGE,"E164")])]});
            var Q67;
            Q67=makeQuery(id+"F1.opExtrude","SWEPT_EDGE",EDGE,{"disambiguationData":[OSD([sQuery(id+"F0.wireOp",EDGE,"E127"),sQuery(id+"F0.wireOp",EDGE,"E162")])]});
            var Q68;
            Q68=makeQuery(id+"F1.opExtrude","SWEPT_EDGE",EDGE,{"disambiguationData":[OSD([sQuery(id+"F0.wireOp",EDGE,"E127"),sQuery(id+"F0.wireOp",EDGE,"E167")])]});
            var Q69;
            Q69=makeQuery(id+"F1.opExtrude","SWEPT_EDGE",EDGE,{"disambiguationData":[OSD([sQuery(id+"F0.wireOp",EDGE,"E154"),sQuery(id+"F0.wireOp",EDGE,"E167")])]});
            var Q70;
            Q70=makeQuery(id+"F1.opExtrude","SWEPT_EDGE",EDGE,{"disambiguationData":[OSD([sQuery(id+"F0.wireOp",EDGE,"E154"),sQuery(id+"F0.wireOp",EDGE,"E162")])]});
            var Q71;
            Q71=makeQuery(id+"F1.opExtrude","SWEPT_EDGE",EDGE,{"disambiguationData":[OSD([sQuery(id+"F0.wireOp",EDGE,"E138"),sQuery(id+"F0.wireOp",EDGE,"E168")])]});
            var Q72;
            Q72=makeQuery(id+"F1.opExtrude","SWEPT_EDGE",EDGE,{"disambiguationData":[OSD([sQuery(id+"F0.wireOp",EDGE,"E160"),sQuery(id+"F0.wireOp",EDGE,"E168")])]});
            var Q73;
            Q73=makeQuery(id+"F1.opExtrude","SWEPT_EDGE",EDGE,{"disambiguationData":[OSD([sQuery(id+"F0.wireOp",EDGE,"E138"),sQuery(id+"F0.wireOp",EDGE,"E163")])]});
            var Q74;
            Q74=makeQuery(id+"F1.opExtrude","SWEPT_EDGE",EDGE,{"disambiguationData":[OSD([sQuery(id+"F0.wireOp",EDGE,"E160"),sQuery(id+"F0.wireOp",EDGE,"E163")])]});
            var Q75;
            Q75=makeQuery(id+"F1.opExtrude","SWEPT_EDGE",EDGE,{"disambiguationData":[OSD([sQuery(id+"F0.wireOp",EDGE,"E184"),sQuery(id+"F0.wireOp",EDGE,"E186")])]});
            var Q76;
            Q76=makeQuery(id+"F1.opExtrude","SWEPT_EDGE",EDGE,{"disambiguationData":[OSD([sQuery(id+"F0.wireOp",EDGE,"E185"),sQuery(id+"F0.wireOp",EDGE,"E187")])]});
            fillet(context, id + "F2", {"entities" : qUnion([Q0, Q1, Q2, Q3, Q4, Q5, Q6, Q7, Q8, Q9, Q10, Q11, Q12, Q13, Q14, Q15, Q16, Q17, Q18, Q19, Q20, Q21, Q22, Q23, Q24, Q25, Q26, Q27, Q28, Q29, Q30, Q31, Q32, Q33, Q34, Q35, Q36, Q37, Q38, Q39, Q40, Q41, Q42, Q43, Q44, Q45, Q46, Q47, Q48, Q49, Q50, Q51, Q52, Q53, Q54, Q55, Q56, Q57, Q58, Q59, Q60, Q61, Q62, Q63, Q64, Q65, Q66, Q67, Q68, Q69, Q70, Q71, Q72, Q73, Q74, Q75, Q76]), "radius" : 0.38 * mm, "tangentPropagation" : true, "allowEdgeOverflow" : false});
        }
        {
            var Q0;
            Q0=makeQuery(id+"F1.opExtrude","SWEPT_EDGE",EDGE,{"disambiguationData":[OSD([sQuery(id+"F0.wireOp",EDGE,"E117"),sQuery(id+"F0.wireOp",EDGE,"E141")])]});
            var Q1;
            Q1=makeQuery(id+"F1.opExtrude","SWEPT_EDGE",EDGE,{"disambiguationData":[OSD([sQuery(id+"F0.wireOp",EDGE,"E107"),sQuery(id+"F0.wireOp",EDGE,"E108")])]});
            var Q2;
            Q2=makeQuery(id+"F1.opExtrude","SWEPT_EDGE",EDGE,{"disambiguationData":[OSD([sQuery(id+"F0.wireOp",EDGE,"E106"),sQuery(id+"F0.wireOp",EDGE,"E144")])]});
            var Q3;
            Q3=makeQuery(id+"F1.opExtrude","SWEPT_EDGE",EDGE,{"disambiguationData":[OSD([sQuery(id+"F0.wireOp",EDGE,"E115"),sQuery(id+"F0.wireOp",EDGE,"E116")])]});
            var Q4;
            Q4=makeQuery(id+"F1.opExtrude","SWEPT_EDGE",EDGE,{"disambiguationData":[OSD([sQuery(id+"F0.wireOp",EDGE,"E117"),sQuery(id+"F0.wireOp",EDGE,"E118")])]});
            var Q5;
            Q5=makeQuery(id+"F1.opExtrude","SWEPT_EDGE",EDGE,{"disambiguationData":[OSD([sQuery(id+"F0.wireOp",EDGE,"E109"),sQuery(id+"F0.wireOp",EDGE,"E110")])]});
            var Q6;
            Q6=makeQuery(id+"F1.opExtrude","SWEPT_EDGE",EDGE,{"disambiguationData":[OSD([sQuery(id+"F0.wireOp",EDGE,"E106"),sQuery(id+"F0.wireOp",EDGE,"E107")])]});
            var Q7;
            Q7=makeQuery(id+"F1.opExtrude","SWEPT_EDGE",EDGE,{"disambiguationData":[OSD([sQuery(id+"F0.wireOp",EDGE,"E104"),sQuery(id+"F0.wireOp",EDGE,"E105")])]});
            var Q8;
            Q8=makeQuery(id+"F1.opExtrude","SWEPT_EDGE",EDGE,{"disambiguationData":[OSD([sQuery(id+"F0.wireOp",EDGE,"E123"),sQuery(id+"F0.wireOp",EDGE,"E124")])]});
            var Q9;
            Q9=makeQuery(id+"F1.opExtrude","SWEPT_EDGE",EDGE,{"disambiguationData":[OSD([sQuery(id+"F0.wireOp",EDGE,"E119"),sQuery(id+"F0.wireOp",EDGE,"E120")])]});
            var Q10;
            Q10=makeQuery(id+"F1.opExtrude","SWEPT_EDGE",EDGE,{"disambiguationData":[OSD([sQuery(id+"F0.wireOp",EDGE,"E97"),sQuery(id+"F0.wireOp",EDGE,"E112")])]});
            var Q11;
            Q11=makeQuery(id+"F1.opExtrude","SWEPT_EDGE",EDGE,{"disambiguationData":[OSD([sQuery(id+"F0.wireOp",EDGE,"E94"),sQuery(id+"F0.wireOp",EDGE,"E95")])]});
            var Q12;
            Q12=makeQuery(id+"F1.opExtrude","SWEPT_EDGE",EDGE,{"disambiguationData":[OSD([sQuery(id+"F0.wireOp",EDGE,"E119"),sQuery(id+"F0.wireOp",EDGE,"E152")])]});
            var Q13;
            Q13=makeQuery(id+"F1.opExtrude","SWEPT_EDGE",EDGE,{"disambiguationData":[OSD([sQuery(id+"F0.wireOp",EDGE,"E120"),sQuery(id+"F0.wireOp",EDGE,"E150")])]});
            var Q14;
            Q14=makeQuery(id+"F1.opExtrude","SWEPT_EDGE",EDGE,{"disambiguationData":[OSD([sQuery(id+"F0.wireOp",EDGE,"E103"),sQuery(id+"F0.wireOp",EDGE,"E146")])]});
            var Q15;
            Q15=makeQuery(id+"F1.opExtrude","SWEPT_EDGE",EDGE,{"disambiguationData":[OSD([sQuery(id+"F0.wireOp",EDGE,"E121"),sQuery(id+"F0.wireOp",EDGE,"E122")])]});
            var Q16;
            Q16=makeQuery(id+"F1.opExtrude","SWEPT_EDGE",EDGE,{"disambiguationData":[OSD([sQuery(id+"F0.wireOp",EDGE,"E102"),sQuery(id+"F0.wireOp",EDGE,"E103")])]});
            var Q17;
            Q17=makeQuery(id+"F1.opExtrude","SWEPT_EDGE",EDGE,{"disambiguationData":[OSD([sQuery(id+"F0.wireOp",EDGE,"E100"),sQuery(id+"F0.wireOp",EDGE,"E101")])]});
            var Q18;
            Q18=makeQuery(id+"F1.opExtrude","SWEPT_EDGE",EDGE,{"disambiguationData":[OSD([sQuery(id+"F0.wireOp",EDGE,"E102"),sQuery(id+"F0.wireOp",EDGE,"E145")])]});
            var Q19;
            Q19=makeQuery(id+"F1.opExtrude","SWEPT_EDGE",EDGE,{"disambiguationData":[OSD([sQuery(id+"F0.wireOp",EDGE,"E113"),sQuery(id+"F0.wireOp",EDGE,"E114")])]});
            var Q20;
            Q20=makeQuery(id+"F1.opExtrude","SWEPT_EDGE",EDGE,{"disambiguationData":[OSD([sQuery(id+"F0.wireOp",EDGE,"E114"),sQuery(id+"F0.wireOp",EDGE,"E153")])]});
            var Q21;
            Q21=makeQuery(id+"F1.opExtrude","SWEPT_EDGE",EDGE,{"disambiguationData":[OSD([sQuery(id+"F0.wireOp",EDGE,"E113"),sQuery(id+"F0.wireOp",EDGE,"E142")])]});
            var Q22;
            Q22=makeQuery(id+"F1.opExtrude","SWEPT_EDGE",EDGE,{"disambiguationData":[OSD([sQuery(id+"F0.wireOp",EDGE,"E125"),sQuery(id+"F0.wireOp",EDGE,"E148")])]});
            var Q23;
            Q23=makeQuery(id+"F1.opExtrude","SWEPT_EDGE",EDGE,{"disambiguationData":[OSD([sQuery(id+"F0.wireOp",EDGE,"E125"),sQuery(id+"F0.wireOp",EDGE,"E126")])]});
            var Q24;
            Q24=makeQuery(id+"F1.opExtrude","SWEPT_EDGE",EDGE,{"disambiguationData":[OSD([sQuery(id+"F0.wireOp",EDGE,"E126"),sQuery(id+"F0.wireOp",EDGE,"E147")])]});
            var Q25;
            Q25=makeQuery(id+"F1.opExtrude","SWEPT_EDGE",EDGE,{"disambiguationData":[OSD([sQuery(id+"F0.wireOp",EDGE,"E92"),sQuery(id+"F0.wireOp",EDGE,"E93")])]});
            var Q26;
            Q26=makeQuery(id+"F1.opExtrude","SWEPT_EDGE",EDGE,{"disambiguationData":[OSD([sQuery(id+"F0.wireOp",EDGE,"E93"),sQuery(id+"F0.wireOp",EDGE,"E143")])]});
            var Q27;
            Q27=makeQuery(id+"F1.opExtrude","SWEPT_EDGE",EDGE,{"disambiguationData":[OSD([sQuery(id+"F0.wireOp",EDGE,"E92"),sQuery(id+"F0.wireOp",EDGE,"E96")])]});
            var Q28;
            Q28=makeQuery(id+"F1.opExtrude","SWEPT_EDGE",EDGE,{"disambiguationData":[OSD([sQuery(id+"F0.wireOp",EDGE,"E111"),sQuery(id+"F0.wireOp",EDGE,"E151")])]});
            var Q29;
            Q29=makeQuery(id+"F1.opExtrude","SWEPT_EDGE",EDGE,{"disambiguationData":[OSD([sQuery(id+"F0.wireOp",EDGE,"E98"),sQuery(id+"F0.wireOp",EDGE,"E111")])]});
            var Q30;
            Q30=makeQuery(id+"F1.opExtrude","SWEPT_EDGE",EDGE,{"disambiguationData":[OSD([sQuery(id+"F0.wireOp",EDGE,"E98"),sQuery(id+"F0.wireOp",EDGE,"E99")])]});
            var Q31;
            Q31=makeQuery(id+"F1.opExtrude","SWEPT_EDGE",EDGE,{"disambiguationData":[OSD([sQuery(id+"F0.wireOp",EDGE,"E99"),sQuery(id+"F0.wireOp",EDGE,"E100")])]});
            var Q32;
            Q32=makeQuery(id+"F1.opExtrude","SWEPT_EDGE",EDGE,{"disambiguationData":[OSD([sQuery(id+"F0.wireOp",EDGE,"E104"),sQuery(id+"F0.wireOp",EDGE,"E147")])]});
            var Q33;
            Q33=makeQuery(id+"F1.opExtrude","SWEPT_EDGE",EDGE,{"disambiguationData":[OSD([sQuery(id+"F0.wireOp",EDGE,"E101"),sQuery(id+"F0.wireOp",EDGE,"E145")])]});
            var Q34;
            Q34=makeQuery(id+"F1.opExtrude","SWEPT_EDGE",EDGE,{"disambiguationData":[OSD([sQuery(id+"F0.wireOp",EDGE,"E94"),sQuery(id+"F0.wireOp",EDGE,"E143")])]});
            var Q35;
            Q35=makeQuery(id+"F1.opExtrude","SWEPT_EDGE",EDGE,{"disambiguationData":[OSD([sQuery(id+"F0.wireOp",EDGE,"E96"),sQuery(id+"F0.wireOp",EDGE,"E112")])]});
            var Q36;
            Q36=makeQuery(id+"F1.opExtrude","SWEPT_EDGE",EDGE,{"disambiguationData":[OSD([sQuery(id+"F0.wireOp",EDGE,"E108"),sQuery(id+"F0.wireOp",EDGE,"E109")])]});
            var Q37;
            Q37=makeQuery(id+"F1.opExtrude","SWEPT_EDGE",EDGE,{"disambiguationData":[OSD([sQuery(id+"F0.wireOp",EDGE,"E116"),sQuery(id+"F0.wireOp",EDGE,"E141")])]});
            var Q38;
            Q38=makeQuery(id+"F1.opExtrude","SWEPT_EDGE",EDGE,{"disambiguationData":[OSD([sQuery(id+"F0.wireOp",EDGE,"E115"),sQuery(id+"F0.wireOp",EDGE,"E142")])]});
            var Q39;
            Q39=makeQuery(id+"F1.opExtrude","SWEPT_EDGE",EDGE,{"disambiguationData":[OSD([sQuery(id+"F0.wireOp",EDGE,"E122"),sQuery(id+"F0.wireOp",EDGE,"E146")])]});
            var Q40;
            Q40=makeQuery(id+"F1.opExtrude","SWEPT_EDGE",EDGE,{"disambiguationData":[OSD([sQuery(id+"F0.wireOp",EDGE,"E97"),sQuery(id+"F0.wireOp",EDGE,"E152")])]});
            var Q41;
            Q41=makeQuery(id+"F1.opExtrude","SWEPT_EDGE",EDGE,{"disambiguationData":[OSD([sQuery(id+"F0.wireOp",EDGE,"E95"),sQuery(id+"F0.wireOp",EDGE,"E150")])]});
            var Q42;
            Q42=makeQuery(id+"F1.opExtrude","SWEPT_EDGE",EDGE,{"disambiguationData":[OSD([sQuery(id+"F0.wireOp",EDGE,"E121"),sQuery(id+"F0.wireOp",EDGE,"E151")])]});
            var Q43;
            Q43=makeQuery(id+"F1.opExtrude","SWEPT_EDGE",EDGE,{"disambiguationData":[OSD([sQuery(id+"F0.wireOp",EDGE,"E123"),sQuery(id+"F0.wireOp",EDGE,"E153")])]});
            var Q44;
            Q44=makeQuery(id+"F1.opExtrude","SWEPT_EDGE",EDGE,{"disambiguationData":[OSD([sQuery(id+"F0.wireOp",EDGE,"E124"),sQuery(id+"F0.wireOp",EDGE,"E149")])]});
            var Q45;
            Q45=makeQuery(id+"F1.opExtrude","SWEPT_EDGE",EDGE,{"disambiguationData":[OSD([sQuery(id+"F0.wireOp",EDGE,"E110"),sQuery(id+"F0.wireOp",EDGE,"E148")])]});
            var Q46;
            Q46=makeQuery(id+"F1.opExtrude","SWEPT_EDGE",EDGE,{"disambiguationData":[OSD([sQuery(id+"F0.wireOp",EDGE,"E118"),sQuery(id+"F0.wireOp",EDGE,"E149")])]});
            var Q47;
            Q47=makeQuery(id+"F1.opExtrude","SWEPT_EDGE",EDGE,{"disambiguationData":[OSD([sQuery(id+"F0.wireOp",EDGE,"E105"),sQuery(id+"F0.wireOp",EDGE,"E144")])]});
            fillet(context, id + "F3", {"entities" : qUnion([Q0, Q1, Q2, Q3, Q4, Q5, Q6, Q7, Q8, Q9, Q10, Q11, Q12, Q13, Q14, Q15, Q16, Q17, Q18, Q19, Q20, Q21, Q22, Q23, Q24, Q25, Q26, Q27, Q28, Q29, Q30, Q31, Q32, Q33, Q34, Q35, Q36, Q37, Q38, Q39, Q40, Q41, Q42, Q43, Q44, Q45, Q46, Q47]), "radius" : 0.38 * mm, "tangentPropagation" : true, "allowEdgeOverflow" : false});
        }
        {
            var Q0;
            Q0=makeQuery(id+"F1.opExtrude","SWEPT_EDGE",EDGE,{"disambiguationData":[OSD([sQuery(id+"F0.wireOp",EDGE,"E132"),sQuery(id+"F0.wireOp",EDGE,"E133")])]});
            var Q1;
            Q1=makeQuery(id+"F1.opExtrude","SWEPT_EDGE",EDGE,{"disambiguationData":[OSD([sQuery(id+"F0.wireOp",EDGE,"E75"),sQuery(id+"F0.wireOp",EDGE,"E133")])]});
            var Q2;
            Q2=makeQuery(id+"F1.opExtrude","SWEPT_EDGE",EDGE,{"disambiguationData":[OSD([sQuery(id+"F0.wireOp",EDGE,"E75"),sQuery(id+"F0.wireOp",EDGE,"E134")])]});
            var Q3;
            Q3=makeQuery(id+"F1.opExtrude","SWEPT_EDGE",EDGE,{"disambiguationData":[OSD([sQuery(id+"F0.wireOp",EDGE,"E71"),sQuery(id+"F0.wireOp",EDGE,"E136")])]});
            fillet(context, id + "F4", {"entities" : qUnion([Q0, Q1, Q2, Q3]), "radius" : 0.38 * mm, "tangentPropagation" : true, "allowEdgeOverflow" : false});
        }
    });
